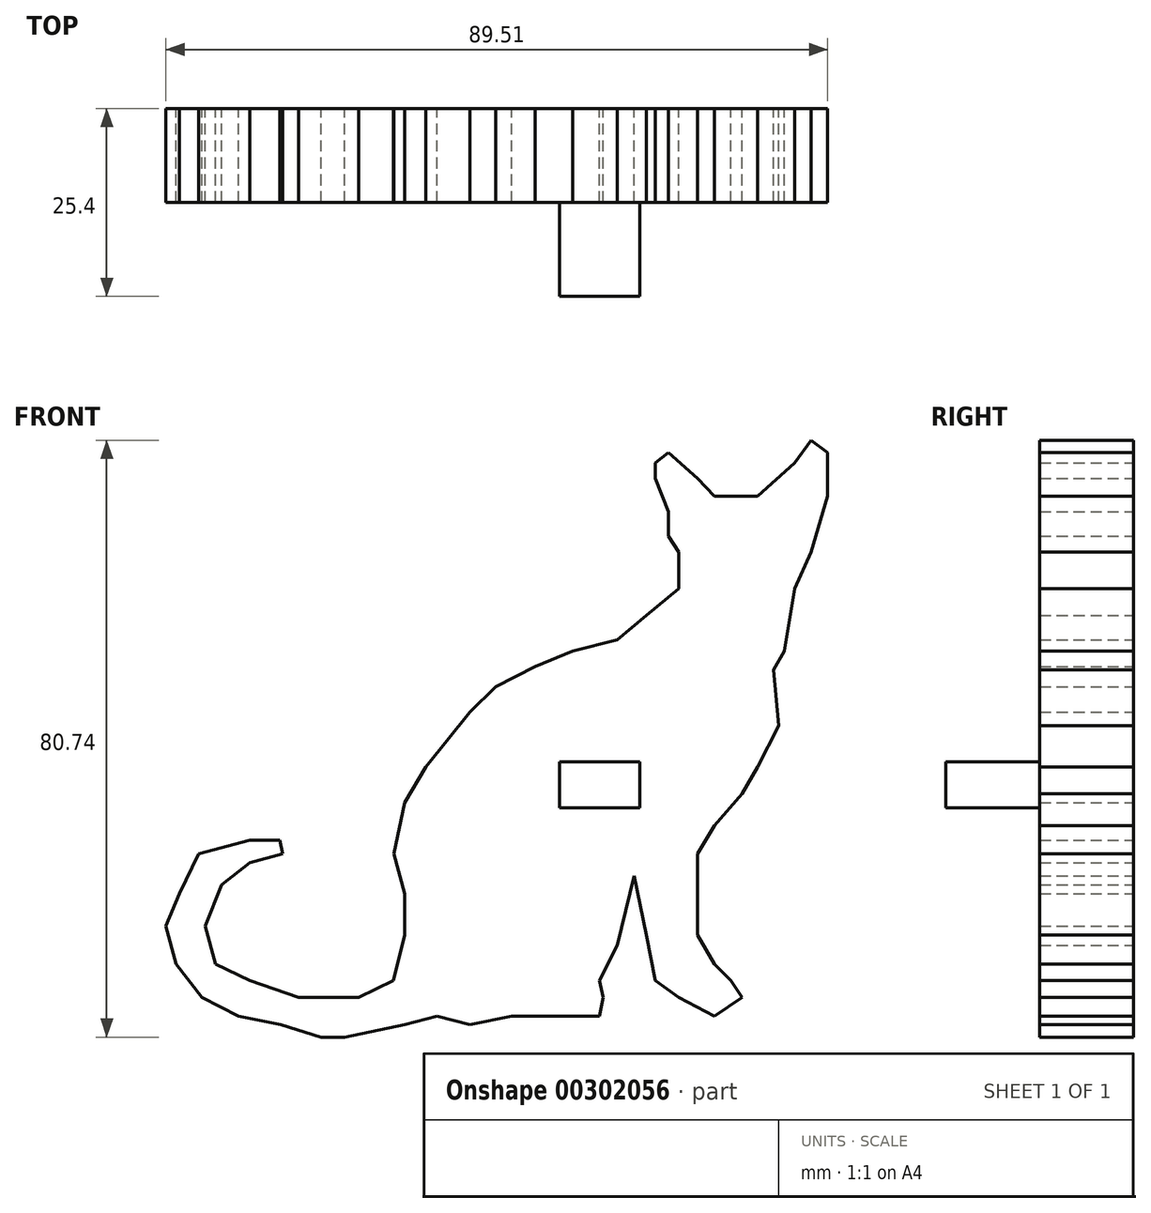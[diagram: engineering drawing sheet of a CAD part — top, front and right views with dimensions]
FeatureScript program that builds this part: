
annotation { "Feature Type Name" : "Feature", "Feature Type Description" : "" }
export const myFeature = defineFeature(function(context is Context, id is Id, definition is map)
    precondition{}
    {
        {
            var Q0;
            Q0=qCreatedBy(makeId("Front.planeOp"),FACE);
            var sketch = newSketch(context, id + "F0", { "sketchPlane" : qUnion([Q0])});
            skLineSegment(sketch, "E0", {"start": v(4.9, 21.2) * mm, "end": v(10.93, 22.72) * mm});
            skLineSegment(sketch, "E1", {"start": v(10.93, 22.72) * mm, "end": v(14.85, 26.03) * mm});
            skLineSegment(sketch, "E2", {"start": v(14.85, 26.03) * mm, "end": v(19.22, 29.65) * mm});
            skLineSegment(sketch, "E3", {"start": v(19.22, 29.65) * mm, "end": v(19.22, 34.63) * mm});
            skLineSegment(sketch, "E4", {"start": v(19.22, 34.63) * mm, "end": v(17.86, 36.74) * mm});
            skLineSegment(sketch, "E5", {"start": v(17.86, 36.74) * mm, "end": v(17.86, 40.05) * mm});
            skLineSegment(sketch, "E6", {"start": v(17.86, 40.05) * mm, "end": v(16.06, 44.58) * mm});
            skLineSegment(sketch, "E7", {"start": v(16.06, 44.58) * mm, "end": v(16.06, 46.69) * mm});
            skLineSegment(sketch, "E8", {"start": v(16.06, 46.69) * mm, "end": v(17.86, 48.04) * mm});
            skLineSegment(sketch, "E9", {"start": v(17.86, 48.04) * mm, "end": v(21.78, 44.58) * mm});
            skLineSegment(sketch, "E10", {"start": v(21.78, 44.58) * mm, "end": v(24.05, 42.16) * mm});
            skLineSegment(sketch, "E11", {"start": v(24.05, 42.16) * mm, "end": v(27.81, 42.16) * mm});
            skLineSegment(sketch, "E12", {"start": v(27.81, 42.16) * mm, "end": v(29.92, 42.16) * mm});
            skLineSegment(sketch, "E13", {"start": v(29.92, 42.16) * mm, "end": v(34.9, 46.69) * mm});
            skLineSegment(sketch, "E14", {"start": v(34.9, 46.69) * mm, "end": v(37.16, 49.7) * mm});
            skLineSegment(sketch, "E15", {"start": v(37.16, 49.7) * mm, "end": v(39.37, 48.04) * mm});
            skLineSegment(sketch, "E16", {"start": v(39.37, 48.04) * mm, "end": v(39.37, 42.16) * mm});
            skLineSegment(sketch, "E17", {"start": v(39.37, 42.16) * mm, "end": v(37.16, 34.63) * mm});
            skLineSegment(sketch, "E18", {"start": v(37.16, 34.63) * mm, "end": v(34.9, 29.65) * mm});
            skLineSegment(sketch, "E19", {"start": v(34.9, 29.65) * mm, "end": v(33.54, 21.2) * mm});
            skLineSegment(sketch, "E20", {"start": v(33.54, 21.2) * mm, "end": v(32.03, 18.65) * mm});
            skLineSegment(sketch, "E21", {"start": v(32.03, 18.65) * mm, "end": v(32.79, 11.1) * mm});
            skLineSegment(sketch, "E22", {"start": v(32.79, 11.1) * mm, "end": v(29.92, 5.53) * mm});
            skLineSegment(sketch, "E23", {"start": v(29.92, 5.53) * mm, "end": v(27.81, 1.91) * mm});
            skLineSegment(sketch, "E24", {"start": v(27.81, 1.91) * mm, "end": v(24.05, -2.46) * mm});
            skLineSegment(sketch, "E25", {"start": v(24.05, -2.46) * mm, "end": v(21.78, -6.23) * mm});
            skLineSegment(sketch, "E26", {"start": v(21.78, -6.23) * mm, "end": v(21.78, -12.1) * mm});
            skLineSegment(sketch, "E27", {"start": v(21.78, -12.1) * mm, "end": v(21.78, -17.23) * mm});
            skLineSegment(sketch, "E28", {"start": v(21.78, -17.23) * mm, "end": v(24.05, -21.15) * mm});
            skLineSegment(sketch, "E29", {"start": v(24.05, -21.15) * mm, "end": v(26.3, -23.41) * mm});
            skLineSegment(sketch, "E30", {"start": v(26.3, -23.41) * mm, "end": v(27.81, -25.67) * mm});
            skLineSegment(sketch, "E31", {"start": v(27.81, -25.67) * mm, "end": v(24.05, -28.18) * mm});
            skLineSegment(sketch, "E32", {"start": v(24.05, -28.18) * mm, "end": v(19.22, -25.67) * mm});
            skLineSegment(sketch, "E33", {"start": v(19.22, -25.67) * mm, "end": v(16.06, -23.41) * mm});
            skLineSegment(sketch, "E34", {"start": v(16.06, -23.41) * mm, "end": v(14.85, -17.23) * mm});
            skLineSegment(sketch, "E35", {"start": v(14.85, -17.23) * mm, "end": v(13.2, -9.24) * mm});
            skLineSegment(sketch, "E36", {"start": v(13.2, -9.24) * mm, "end": v(10.93, -18.59) * mm});
            skLineSegment(sketch, "E37", {"start": v(10.93, -18.59) * mm, "end": v(8.52, -23.41) * mm});
            skLineSegment(sketch, "E38", {"start": v(8.52, -23.41) * mm, "end": v(8.99, -25.67) * mm});
            skLineSegment(sketch, "E39", {"start": v(8.99, -25.67) * mm, "end": v(8.52, -28.18) * mm});
            skLineSegment(sketch, "E40", {"start": v(8.52, -28.18) * mm, "end": v(1.58, -28.18) * mm});
            skLineSegment(sketch, "E41", {"start": v(1.58, -28.18) * mm, "end": v(-3.4, -28.18) * mm});
            skLineSegment(sketch, "E42", {"start": v(-3.4, -28.18) * mm, "end": v(-9.04, -29.36) * mm});
            skLineSegment(sketch, "E43", {"start": v(-9.04, -29.36) * mm, "end": v(-13.5, -28.18) * mm});
            skLineSegment(sketch, "E44", {"start": v(-13.5, -28.18) * mm, "end": v(-17.86, -29.36) * mm});
            skLineSegment(sketch, "E45", {"start": v(-17.86, -29.36) * mm, "end": v(-24.04, -30.64) * mm});
            skLineSegment(sketch, "E46", {"start": v(-24.04, -30.64) * mm, "end": v(-25.98, -31.04) * mm});
            skLineSegment(sketch, "E47", {"start": v(-25.98, -31.04) * mm, "end": v(-29.17, -31.04) * mm});
            skLineSegment(sketch, "E48", {"start": v(-29.17, -31.04) * mm, "end": v(-34.6, -29.36) * mm});
            skLineSegment(sketch, "E49", {"start": v(-34.6, -29.36) * mm, "end": v(-40.32, -28.18) * mm});
            skLineSegment(sketch, "E50", {"start": v(-40.32, -28.18) * mm, "end": v(-45.3, -25.67) * mm});
            skLineSegment(sketch, "E51", {"start": v(-45.3, -25.67) * mm, "end": v(-48.76, -21.15) * mm});
            skLineSegment(sketch, "E52", {"start": v(-48.76, -21.15) * mm, "end": v(-50.14, -16) * mm});
            skLineSegment(sketch, "E53", {"start": v(-50.14, -16) * mm, "end": v(-48.31, -11.65) * mm});
            skLineSegment(sketch, "E54", {"start": v(-48.31, -11.65) * mm, "end": v(-45.75, -6.23) * mm});
            skLineSegment(sketch, "E55", {"start": v(-45.75, -6.23) * mm, "end": v(-38.8, -4.37) * mm});
            skLineSegment(sketch, "E56", {"start": v(-38.8, -4.37) * mm, "end": v(-34.75, -4.37) * mm});
            skLineSegment(sketch, "E57", {"start": v(-34.75, -4.37) * mm, "end": v(-34.36, -6.23) * mm});
            skLineSegment(sketch, "E58", {"start": v(-34.36, -6.23) * mm, "end": v(-38.8, -7.42) * mm});
            skLineSegment(sketch, "E59", {"start": v(-38.8, -7.42) * mm, "end": v(-42.58, -10.45) * mm});
            skLineSegment(sketch, "E60", {"start": v(-42.58, -10.45) * mm, "end": v(-44.85, -16) * mm});
            skLineSegment(sketch, "E61", {"start": v(-44.85, -16) * mm, "end": v(-43.47, -21.15) * mm});
            skLineSegment(sketch, "E62", {"start": v(-43.47, -21.15) * mm, "end": v(-38.8, -23.41) * mm});
            skLineSegment(sketch, "E63", {"start": v(-38.8, -23.41) * mm, "end": v(-32.18, -25.67) * mm});
            skLineSegment(sketch, "E64", {"start": v(-32.18, -25.67) * mm, "end": v(-24.04, -25.67) * mm});
            skLineSegment(sketch, "E65", {"start": v(-24.04, -25.67) * mm, "end": v(-19.37, -23.41) * mm});
            skLineSegment(sketch, "E66", {"start": v(-19.37, -23.41) * mm, "end": v(-17.86, -17.23) * mm});
            skLineSegment(sketch, "E67", {"start": v(-17.86, -17.23) * mm, "end": v(-17.86, -11.65) * mm});
            skLineSegment(sketch, "E68", {"start": v(-17.86, -11.65) * mm, "end": v(-19.32, -6.23) * mm});
            skLineSegment(sketch, "E69", {"start": v(-19.32, -6.23) * mm, "end": v(-17.86, 0.7) * mm});
            skLineSegment(sketch, "E70", {"start": v(-17.86, 0.7) * mm, "end": v(-15, 5.53) * mm});
            skLineSegment(sketch, "E71", {"start": v(-15, 5.53) * mm, "end": v(-9.04, 12.92) * mm});
            skLineSegment(sketch, "E72", {"start": v(-9.04, 12.92) * mm, "end": v(-5.5, 16.39) * mm});
            skLineSegment(sketch, "E73", {"start": v(-5.5, 16.39) * mm, "end": v(-0.22, 19.1) * mm});
            skLineSegment(sketch, "E74", {"start": v(-0.22, 19.1) * mm, "end": v(4.9, 21.2) * mm});
            skSolve(sketch);
        }
        {
            var Q0;
            {var subQ7=sQuery(id+"F0.wireOp",EDGE,"E0");Q0=makeQuery(id+"F0.imprint","IMPRINT",FACE,{"disambiguationData":[TD([[makeQuery(id+"F0.imprint","IMPRINT",EDGE,{"derivedFrom":subQ7}),-1.0]])]});}
            var Q1;
            {var subQ4=sQuery(id+"F0.wireOp",EDGE,"E70");Q1=makeQuery(id+"F0.imprint","IMPRINT",FACE,{"disambiguationData":[TD([[makeQuery(id+"F0.imprint","IMPRINT",EDGE,{"derivedFrom":subQ4}),-1.0]])]});}
            extrude(context, id + "F1", {"entities" : qUnion([Q0, Q1]), "depth" : 12.7 * mm});
        }
        {
            var Q0;
            Q0=makeQuery(id+"F1.opExtrude","CAP_FACE",FACE,{"disambiguationData":[OSD([sQuery(id+"F0.wireOp",EDGE,"E0"),sQuery(id+"F0.wireOp",EDGE,"E1"),sQuery(id+"F0.wireOp",EDGE,"E2"),sQuery(id+"F0.wireOp",EDGE,"E3"),sQuery(id+"F0.wireOp",EDGE,"E4"),sQuery(id+"F0.wireOp",EDGE,"E5"),sQuery(id+"F0.wireOp",EDGE,"E6"),sQuery(id+"F0.wireOp",EDGE,"E7"),sQuery(id+"F0.wireOp",EDGE,"E8"),sQuery(id+"F0.wireOp",EDGE,"E9"),sQuery(id+"F0.wireOp",EDGE,"E10"),sQuery(id+"F0.wireOp",EDGE,"E11"),sQuery(id+"F0.wireOp",EDGE,"E12"),sQuery(id+"F0.wireOp",EDGE,"E13"),sQuery(id+"F0.wireOp",EDGE,"E14"),sQuery(id+"F0.wireOp",EDGE,"E15"),sQuery(id+"F0.wireOp",EDGE,"E16"),sQuery(id+"F0.wireOp",EDGE,"E17"),sQuery(id+"F0.wireOp",EDGE,"E18"),sQuery(id+"F0.wireOp",EDGE,"E19"),sQuery(id+"F0.wireOp",EDGE,"E20"),sQuery(id+"F0.wireOp",EDGE,"E21"),sQuery(id+"F0.wireOp",EDGE,"E22"),sQuery(id+"F0.wireOp",EDGE,"E23"),sQuery(id+"F0.wireOp",EDGE,"E24"),sQuery(id+"F0.wireOp",EDGE,"E25"),sQuery(id+"F0.wireOp",EDGE,"E26"),sQuery(id+"F0.wireOp",EDGE,"E27"),sQuery(id+"F0.wireOp",EDGE,"E28"),sQuery(id+"F0.wireOp",EDGE,"E29"),sQuery(id+"F0.wireOp",EDGE,"E30"),sQuery(id+"F0.wireOp",EDGE,"E31"),sQuery(id+"F0.wireOp",EDGE,"E32"),sQuery(id+"F0.wireOp",EDGE,"E33"),sQuery(id+"F0.wireOp",EDGE,"E34"),sQuery(id+"F0.wireOp",EDGE,"E35"),sQuery(id+"F0.wireOp",EDGE,"E36"),sQuery(id+"F0.wireOp",EDGE,"E37"),sQuery(id+"F0.wireOp",EDGE,"E38"),sQuery(id+"F0.wireOp",EDGE,"E39"),sQuery(id+"F0.wireOp",EDGE,"E40"),sQuery(id+"F0.wireOp",EDGE,"E41"),sQuery(id+"F0.wireOp",EDGE,"E42"),sQuery(id+"F0.wireOp",EDGE,"E43"),sQuery(id+"F0.wireOp",EDGE,"E44"),sQuery(id+"F0.wireOp",EDGE,"E45"),sQuery(id+"F0.wireOp",EDGE,"E46"),sQuery(id+"F0.wireOp",EDGE,"E47"),sQuery(id+"F0.wireOp",EDGE,"E48"),sQuery(id+"F0.wireOp",EDGE,"E49"),sQuery(id+"F0.wireOp",EDGE,"E50"),sQuery(id+"F0.wireOp",EDGE,"E51"),sQuery(id+"F0.wireOp",EDGE,"E52"),sQuery(id+"F0.wireOp",EDGE,"E53"),sQuery(id+"F0.wireOp",EDGE,"E54"),sQuery(id+"F0.wireOp",EDGE,"E55"),sQuery(id+"F0.wireOp",EDGE,"E56"),sQuery(id+"F0.wireOp",EDGE,"E57"),sQuery(id+"F0.wireOp",EDGE,"E58"),sQuery(id+"F0.wireOp",EDGE,"E59"),sQuery(id+"F0.wireOp",EDGE,"E60"),sQuery(id+"F0.wireOp",EDGE,"E61"),sQuery(id+"F0.wireOp",EDGE,"E62"),sQuery(id+"F0.wireOp",EDGE,"E63"),sQuery(id+"F0.wireOp",EDGE,"E64"),sQuery(id+"F0.wireOp",EDGE,"E65"),sQuery(id+"F0.wireOp",EDGE,"E66"),sQuery(id+"F0.wireOp",EDGE,"E67"),sQuery(id+"F0.wireOp",EDGE,"E68"),sQuery(id+"F0.wireOp",EDGE,"E69"),sQuery(id+"F0.wireOp",EDGE,"E70"),sQuery(id+"F0.wireOp",EDGE,"E71"),sQuery(id+"F0.wireOp",EDGE,"E72"),sQuery(id+"F0.wireOp",EDGE,"E73"),sQuery(id+"F0.wireOp",EDGE,"E74")])],"isStart":false});
            var sketch = newSketch(context, id + "F2", { "sketchPlane" : qUnion([Q0])});
            skLineSegment(sketch, "E75", {"start": v(3.1, 6.2) * mm, "end": v(13.96, 6.2) * mm});
            skLineSegment(sketch, "E76", {"start": v(13.96, 6.2) * mm, "end": v(13.96, 0) * mm});
            skLineSegment(sketch, "E77", {"start": v(3.1, 6.2) * mm, "end": v(3.1, 0) * mm});
            skLineSegment(sketch, "E78", {"start": v(3.1, 0) * mm, "end": v(13.96, 0) * mm});
            skSolve(sketch);
        }
        {
            var Q0;
            Q0 = qSketchRegion(id + "F2", true);
            extrude(context, id + "F3", {"entities" : qUnion([Q0]), "operationType" : NewBodyOperationType.ADD, "depth" : 12.7 * mm});
        }
    });
